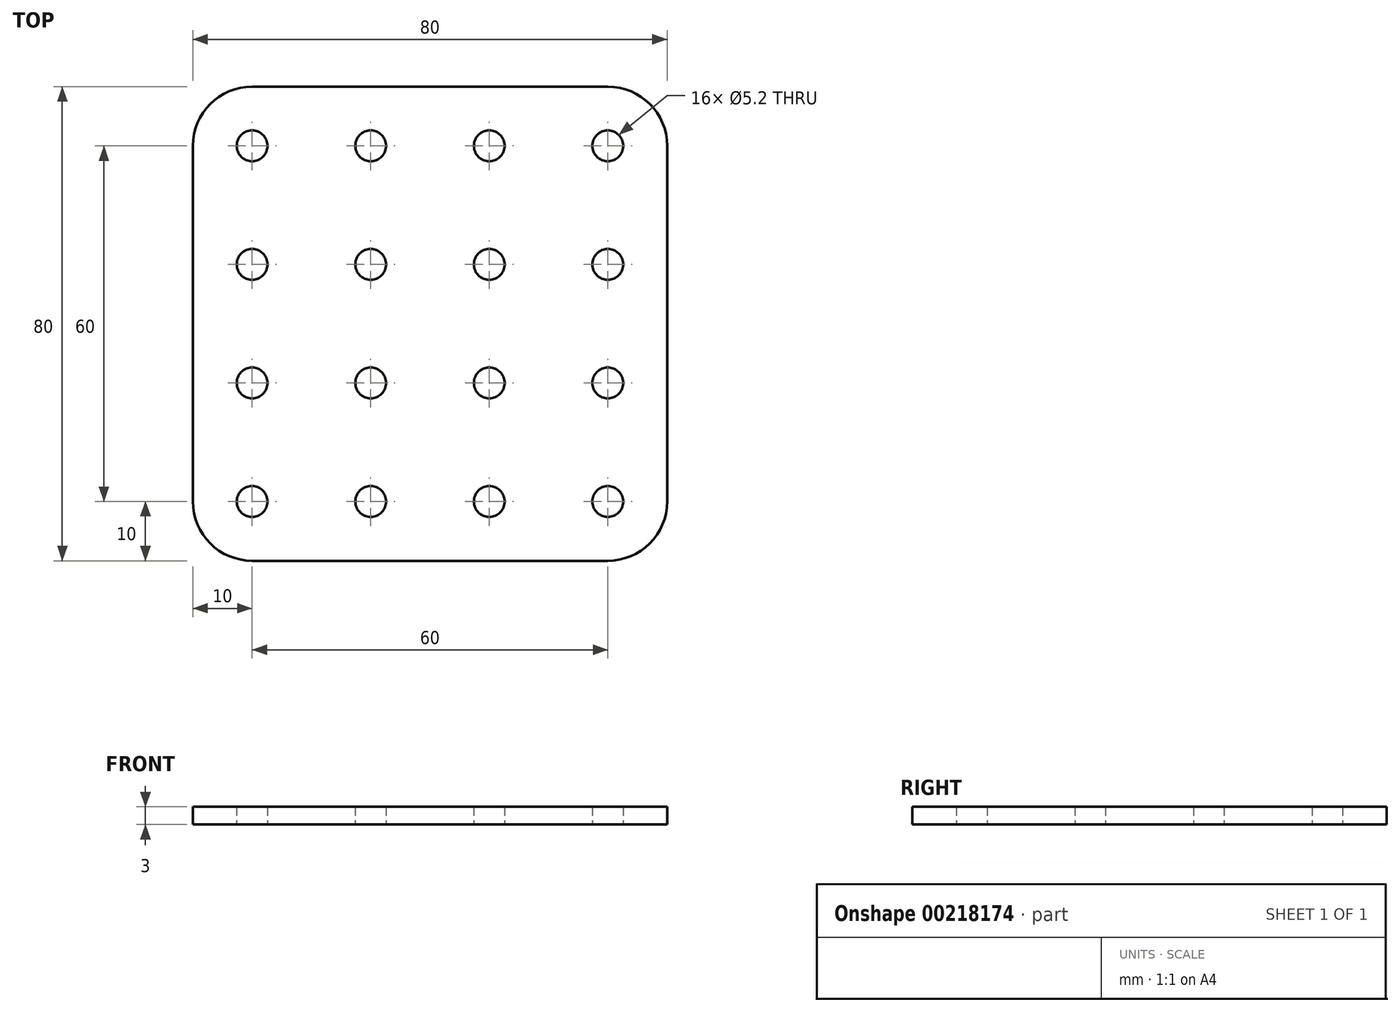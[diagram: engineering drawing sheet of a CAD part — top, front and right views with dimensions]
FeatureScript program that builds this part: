
annotation { "Feature Type Name" : "Feature", "Feature Type Description" : "" }
export const myFeature = defineFeature(function(context is Context, id is Id, definition is map)
    precondition{}
    {
        {
            var Q0;
            Q0=qCreatedBy(makeId("Top.planeOp"),FACE);
            var sketch = newSketch(context, id + "F0", { "sketchPlane" : qUnion([Q0])});
            skPoint(sketch, "E0", {"position": v(-30, 30) * mm});
            skPoint(sketch, "E1.0.1.0", {"position": v(-30, 10) * mm});
            skPoint(sketch, "E1.0.2.0", {"position": v(-30, -10) * mm});
            skPoint(sketch, "E1.0.3.0", {"position": v(-30, -30) * mm});
            skPoint(sketch, "E1.1.0.0", {"position": v(-10, 30) * mm});
            skPoint(sketch, "E1.1.1.0", {"position": v(-10, 10) * mm});
            skPoint(sketch, "E1.1.2.0", {"position": v(-10, -10) * mm});
            skPoint(sketch, "E1.1.3.0", {"position": v(-10, -30) * mm});
            skPoint(sketch, "E1.2.0.0", {"position": v(10, 30) * mm});
            skPoint(sketch, "E1.2.1.0", {"position": v(10, 10) * mm});
            skPoint(sketch, "E1.2.2.0", {"position": v(10, -10) * mm});
            skPoint(sketch, "E1.2.3.0", {"position": v(10, -30) * mm});
            skPoint(sketch, "E1.3.0.0", {"position": v(30, 30) * mm});
            skPoint(sketch, "E1.3.1.0", {"position": v(30, 10) * mm});
            skPoint(sketch, "E1.3.2.0", {"position": v(30, -10) * mm});
            skPoint(sketch, "E1.3.3.0", {"position": v(30, -30) * mm});
            skLineSegment(sketch, "E1.direction1", {"start": v(-30, 30) * mm, "end": v(-10, 30) * mm, "construction": true});
            skLineSegment(sketch, "E1.direction2", {"start": v(-30, 30) * mm, "end": v(-30, 10) * mm, "construction": true});
            skLineSegment(sketch, "E2.bottom", {"start": v(-40, 40) * mm, "end": v(40, 40) * mm});
            skLineSegment(sketch, "E2.top", {"start": v(-40, -40) * mm, "end": v(40, -40) * mm});
            skLineSegment(sketch, "E2.left", {"start": v(-40, 40) * mm, "end": v(-40, -40) * mm});
            skLineSegment(sketch, "E2.right", {"start": v(40, 40) * mm, "end": v(40, -40) * mm});
            skPoint(sketch, "E3", {"position": v(0, 40) * mm});
            skPoint(sketch, "E4", {"position": v(40, 0) * mm});
            skSolve(sketch);
        }
        {
            var Q0;
            Q0=makeQuery(id+"F0.imprint","IMPRINT",FACE,{"disambiguationData":[TD([[makeQuery(id+"F0.imprint","IMPRINT",EDGE,{"derivedFrom":sQuery(id+"F0.wireOp",EDGE,"E2.bottom")}),-1.0]])]});
            extrude(context, id + "F1", {"entities" : qUnion([Q0]), "depth" : 3 * mm});
        }
        {
            var Q0;
            Q0=sQuery(id+"F0.wireOp",VERTEX,"E1.direction1.start");
            var Q1;
            Q1=sQuery(id+"F0.wireOp",VERTEX,"E1.direction1.end");
            var Q2;
            Q2=sQuery(id+"F0.wireOp",VERTEX,"E1.2.0.0");
            var Q3;
            Q3=sQuery(id+"F0.wireOp",VERTEX,"E1.3.0.0");
            var Q4;
            Q4=sQuery(id+"F0.wireOp",VERTEX,"E1.3.1.0");
            var Q5;
            Q5=sQuery(id+"F0.wireOp",VERTEX,"E1.2.1.0");
            var Q6;
            Q6=sQuery(id+"F0.wireOp",VERTEX,"E1.1.1.0");
            var Q7;
            Q7=sQuery(id+"F0.wireOp",VERTEX,"E1.0.1.0");
            var Q8;
            Q8=sQuery(id+"F0.wireOp",VERTEX,"E1.0.2.0");
            var Q9;
            Q9=sQuery(id+"F0.wireOp",VERTEX,"E1.1.2.0");
            var Q10;
            Q10=sQuery(id+"F0.wireOp",VERTEX,"E1.2.2.0");
            var Q11;
            Q11=sQuery(id+"F0.wireOp",VERTEX,"E1.3.2.0");
            var Q12;
            Q12=sQuery(id+"F0.wireOp",VERTEX,"E1.3.3.0");
            var Q13;
            Q13=sQuery(id+"F0.wireOp",VERTEX,"E1.2.3.0");
            var Q14;
            Q14=sQuery(id+"F0.wireOp",VERTEX,"E1.1.3.0");
            var Q15;
            Q15=sQuery(id+"F0.wireOp",VERTEX,"E1.0.3.0");
            var Q16;
            Q16=makeQuery(id+"F1.opExtrude","SWEPT_BODY",BODY,{"disambiguationData":[OSD([sQuery(id+"F0.wireOp",EDGE,"E2.bottom"),sQuery(id+"F0.wireOp",EDGE,"E2.top"),sQuery(id+"F0.wireOp",EDGE,"E2.left"),sQuery(id+"F0.wireOp",EDGE,"E2.right")])]});
            hole(context, id + "F2", {"style" : HoleStyle.SIMPLE, "endStyle" : HoleEndStyle.THROUGH, "oppositeDirection" : true, "holeDiameter" : 5.2 * mm, "startFromSketch" : true, "locations" : qUnion([Q0, Q1, Q2, Q3, Q4, Q5, Q6, Q7, Q8, Q9, Q10, Q11, Q12, Q13, Q14, Q15]), "scope" : qUnion([Q16]), "isTappedThrough" : true});
        }
        {
            var Q0;
            Q0=makeQuery(id+"F1.opExtrude","SWEPT_EDGE",EDGE,{"disambiguationData":[OSD([sQuery(id+"F0.wireOp",EDGE,"E2.bottom"),sQuery(id+"F0.wireOp",EDGE,"E2.right")])]});
            var Q1;
            Q1=makeQuery(id+"F1.opExtrude","SWEPT_EDGE",EDGE,{"disambiguationData":[OSD([sQuery(id+"F0.wireOp",EDGE,"E2.bottom"),sQuery(id+"F0.wireOp",EDGE,"E2.left")])]});
            var Q2;
            Q2=makeQuery(id+"F1.opExtrude","SWEPT_EDGE",EDGE,{"disambiguationData":[OSD([sQuery(id+"F0.wireOp",EDGE,"E2.top"),sQuery(id+"F0.wireOp",EDGE,"E2.left")])]});
            var Q3;
            Q3=makeQuery(id+"F1.opExtrude","SWEPT_EDGE",EDGE,{"disambiguationData":[OSD([sQuery(id+"F0.wireOp",EDGE,"E2.top"),sQuery(id+"F0.wireOp",EDGE,"E2.right")])]});
            fillet(context, id + "F3", {"entities" : qUnion([Q0, Q1, Q2, Q3]), "radius" : 10 * mm, "tangentPropagation" : true, "allowEdgeOverflow" : false});
        }
    });
